# Revit family: Mittenabhängung GKS 50 07 FS, GKS 50 07 FS SP,GKS 50 11 FS, GKS 50 07 FT, GKS 50 11 FT
name_source: partatom
category: Generic Models
revit_build: Autodesk Revit 2017 (Build: 20160225_1515(x64)
units: mm (PartAtom-declared; Revit-internal decimal feet)

## family parameters
Always vertical = Yes
Can host rebar = No
Cut with Voids When Loaded = No
Part Type = Normal
Room Calculation Point = No
Round Connector Dimension = Use Diameter
Shared = No
Work Plane-Based = No

## types (6) — shared parameters
Manufacturer = OBO Bettermann
Type Image = <None>
URL = http://www.obo-bettermann.com
Width = 60 mm  [stored 0.19685 ft]
Width 1 = 40 mm  [stored 0.131234 ft]
Width/2 = 30 mm  [stored 0.0984252 ft]

## per-type parameters (varying)
| type | Diameter | GTIN | Manufacturer Art.No. | Material |
| GKS 50 07 FS | 7 mm  [stored 0.0229659 ft] | 4012196421398 | 6015263 | Strip-galvanised |
| GKS 50 07 FS SP | 7 mm  [stored 0.0229659 ft] | 4012196661930 | 6015290 | Strip-galvanised |
| GKS 50 11 FS | 11 mm  [stored 0.0360892 ft] | 4012196965847 | 6015276 | Strip-galvanised |
| GKS 50 07 FT | 7 mm  [stored 0.0229659 ft] | 4012196785353 | 6015271 | Hot-dip galvanised |
| GKS 50 11 FT | 11 mm  [stored 0.0360892 ft] | 4012196965908 | 6015278 | Hot-dip galvanised |
| GKS 50 11 A4 | 11 mm  [stored 0.0360892 ft] | 4012196937394 | 6015280 | Stainless steel, A4 |

note: column(s) folded — value = type name in every type: Article Type

note: [stored X ft] marks values corroborated as IEEE doubles in the binary element streams (Revit-internal decimal feet)

## geometry (parser evidence)
native form markers: Sweep x2
no freeform markers — native parametric forms only
